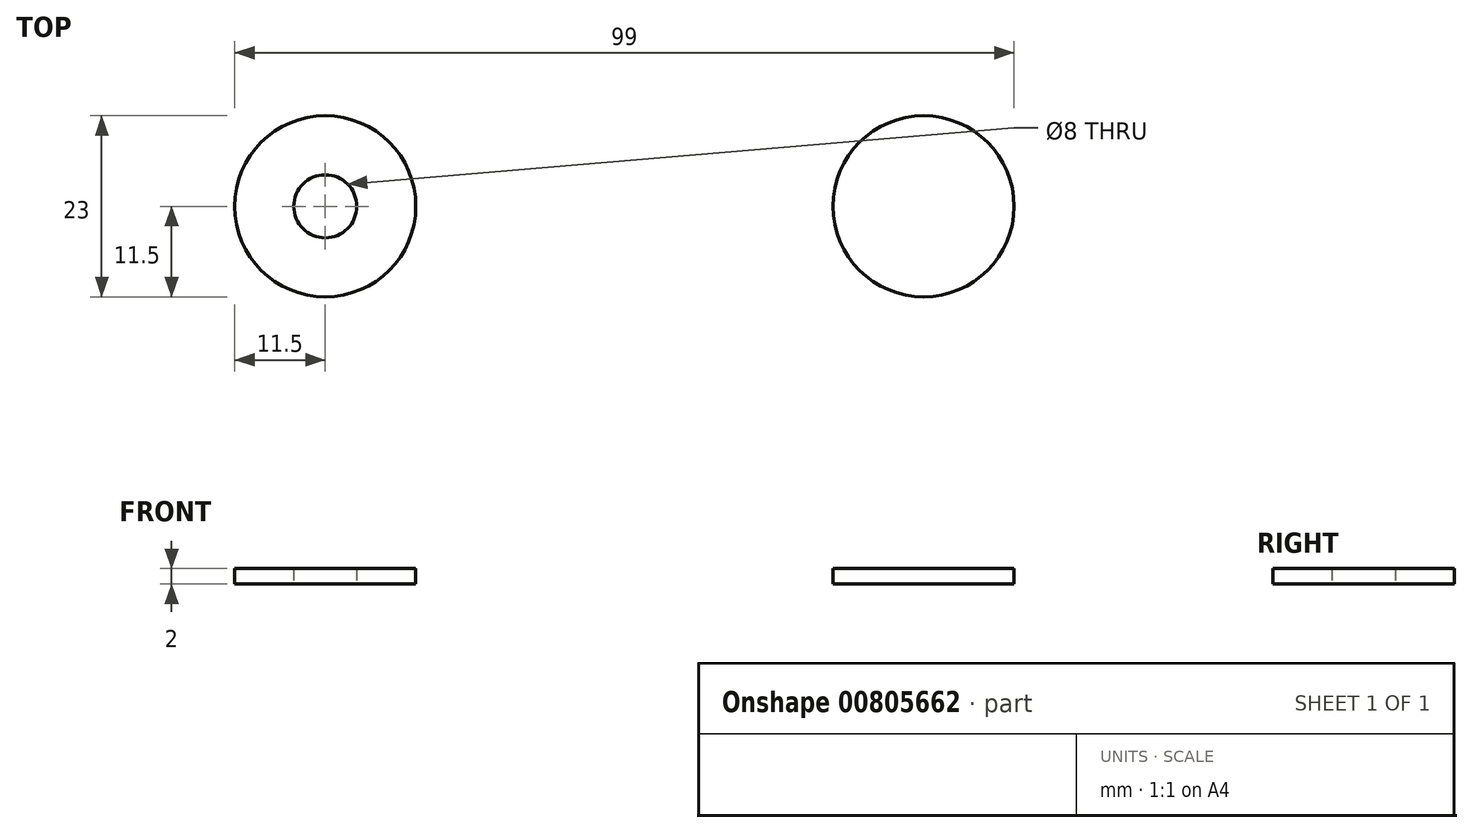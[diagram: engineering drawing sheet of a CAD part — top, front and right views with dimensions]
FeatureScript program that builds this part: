
annotation { "Feature Type Name" : "Feature", "Feature Type Description" : "" }
export const myFeature = defineFeature(function(context is Context, id is Id, definition is map)
    precondition{}
    {
        {
            var Q0;
            Q0=qCreatedBy(makeId("Top.planeOp"),FACE);
            var sketch = newSketch(context, id + "F0", { "sketchPlane" : qUnion([Q0])});
            skLineSegment(sketch, "E0", {"start": v(0, 0) * mm, "end": v(38, 0) * mm});
            skCircle(sketch, "E1", {"center": v(38, 0) * mm, "radius": 4 * mm});
            skCircle(sketch, "E2", {"center": v(38, 0) * mm, "radius": 11.5 * mm});
            skCircle(sketch, "E3.MirrorC", {"center": v(-38, 0) * mm, "radius": 4 * mm});
            skCircle(sketch, "E4.MirrorC", {"center": v(-38, 0) * mm, "radius": 11.5 * mm});
            skSolve(sketch);
        }
        {
            var Q0;
            Q0=qSketchRegion(id+"F0",true);
            var Q1;
            Q1=makeQuery(id+"F0.imprint","IMPRINT",FACE,{"disambiguationData":[TD([[makeQuery(id+"F0.imprint","IMPRINT",EDGE,{"derivedFrom":sQuery(id+"F0.wireOp",EDGE,"E3.MirrorC")}),-1.0]])]});
            var Q2;
            Q2=makeQuery(id+"F0.imprint","IMPRINT",FACE,{"disambiguationData":[TD([[makeQuery(id+"F0.imprint","IMPRINT",EDGE,{"derivedFrom":sQuery(id+"F0.wireOp",EDGE,"E1")}),1.0]])]});
            extrude(context, id + "F1", {"entities" : qUnion([Q0, Q1, Q2]), "depth" : 2 * mm, "offsetDistance" : 25 * mm});
        }
        {
            var Q0;
            Q0=sQuery(id+"F0.wireOp",EDGE,"E3.MirrorC");
            var Q1;
            Q1=sQuery(id+"F0.wireOp",EDGE,"E1");
            extrude(context, id + "F2", {"bodyType" : ToolBodyType.SURFACE, "surfaceEntities" : qUnion([Q0, Q1]), "depth" : 7 * mm, "offsetDistance" : 25 * mm});
        }
    });
